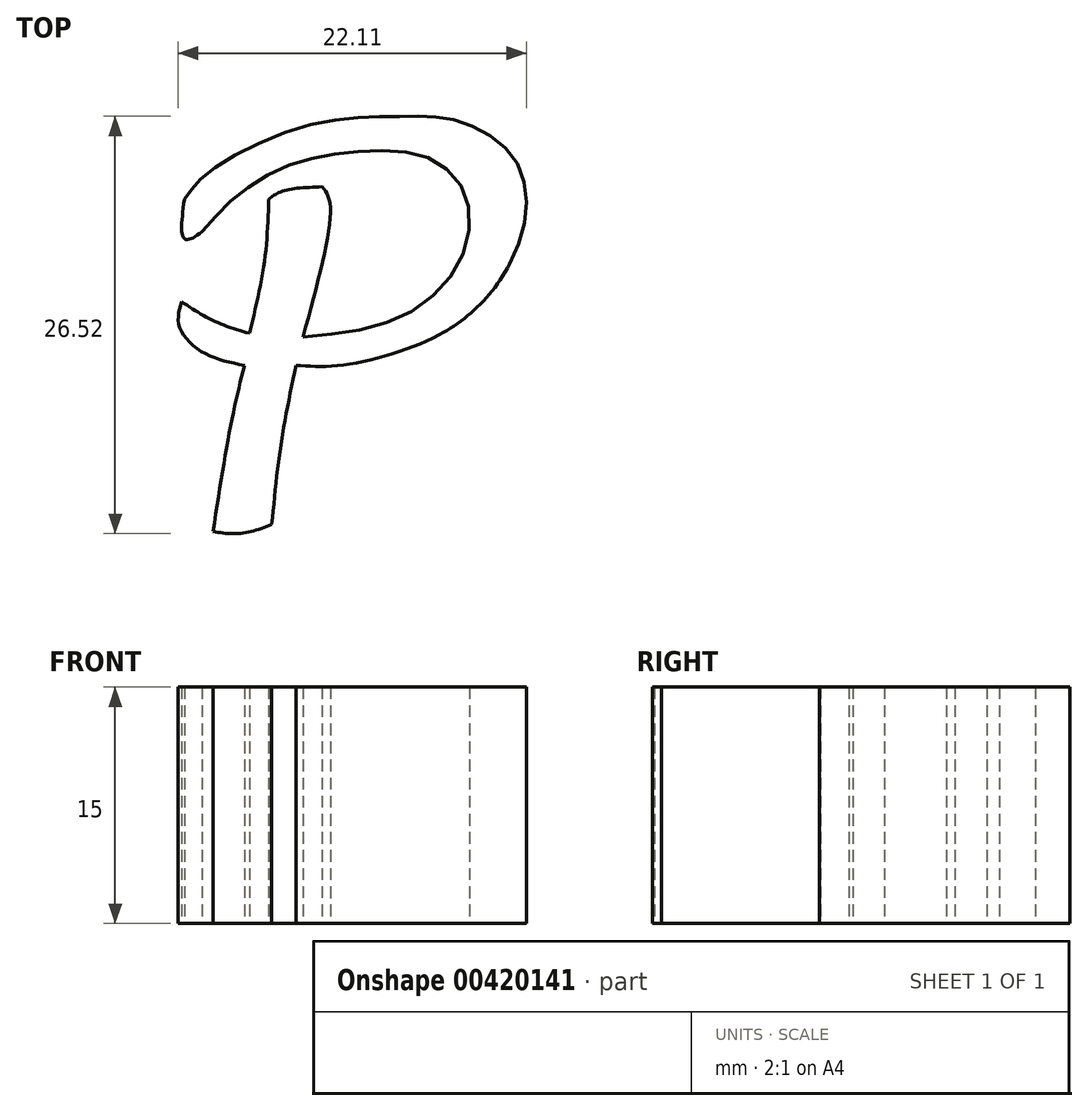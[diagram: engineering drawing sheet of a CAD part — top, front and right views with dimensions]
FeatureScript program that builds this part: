
annotation { "Feature Type Name" : "Feature", "Feature Type Description" : "" }
export const myFeature = defineFeature(function(context is Context, id is Id, definition is map)
    precondition{}
    {
        {
            var Q0;
            Q0=qCreatedBy(makeId("Top.planeOp"),FACE);
            var sketch = newSketch(context, id + "F0", { "sketchPlane" : qUnion([Q0])});
            skFitSpline(sketch, "E0", {"points": [v(-29.52, 16.09) * mm, v(-21.73, 24.17) * mm, v(-15.95, 22) * mm], "startDerivative": vector(5.63, 25.07) * mm, "endDerivative": vector(12.64, -16.05) * mm});
            skFitSpline(sketch, "E1", {"points": [v(-29.52, 16.09) * mm, v(-29.52, 11.79) * mm, v(-26.49, 8.08) * mm, v(-18.6, 8.9) * mm, v(-11.86, 14.14) * mm], "startDerivative": vector(-2.65, -20.74) * mm, "endDerivative": vector(20.85, 20.56) * mm});
            skFitSpline(sketch, "E2", {"points": [v(-15.95, 22) * mm, v(-15.95, 19.53) * mm, v(-19.6, 15.68) * mm, v(-26.31, 14.5) * mm], "startDerivative": vector(1.91, -9.63) * mm, "endDerivative": vector(-17.6, -0.63) * mm});
            skFitSpline(sketch, "E3", {"points": [v(-26.31, 14.5) * mm, v(-26.31, 12.31) * mm, v(-24.25, 10.14) * mm, v(-18.22, 11.13) * mm, v(-11.16, 17.2) * mm], "startDerivative": vector(-1.95, -12.78) * mm, "endDerivative": vector(19.15, 20.18) * mm});
            skFitSpline(sketch, "E4", {"points": [v(-11.16, 17.2) * mm, v(-8.94, 21.18) * mm, v(-5, 24.17) * mm, v(-0.8, 24.22) * mm, v(2.15, 22.9) * mm], "startDerivative": vector(7.17, 15.76) * mm, "endDerivative": vector(12.55, -6.92) * mm});
            skFitSpline(sketch, "E5", {"points": [v(2.15, 22.9) * mm, v(2.96, 23.95) * mm, v(5.9, 24.4) * mm], "startDerivative": vector(1.46, 2.97) * mm, "endDerivative": vector(5.76, 0.2) * mm});
            skFitSpline(sketch, "E6", {"points": [v(-11.86, 14.14) * mm, v(-11.86, 10.9) * mm, v(-9.94, 8.05) * mm, v(-6.14, 8.37) * mm], "startDerivative": vector(-1.2, -9.86) * mm, "endDerivative": vector(11.9, 3.41) * mm});
            skFitSpline(sketch, "E7", {"points": [v(-6.14, 8.37) * mm, v(-2.1, 12.17) * mm, v(0.93, 17.2) * mm], "startDerivative": vector(8.72, 7.18) * mm, "endDerivative": vector(5.42, 10.46) * mm});
            skFitSpline(sketch, "E8", {"points": [v(0.93, 17.2) * mm, v(0.93, 11.63) * mm, v(3.05, 8.96) * mm, v(6.72, 9.41) * mm, v(12.48, 14.14) * mm], "startDerivative": vector(-2.53, -22.33) * mm, "endDerivative": vector(18.4, 18.48) * mm});
            skFitSpline(sketch, "E9", {"points": [v(5.9, 24.4) * mm, v(4.28, 19.57) * mm, v(4.12, 12.84) * mm, v(5.03, 11.7) * mm, v(7.94, 12.57) * mm, v(12.9, 17.2) * mm], "startDerivative": vector(-8.65, -19.72) * mm, "endDerivative": vector(19.75, 21.62) * mm});
            skFitSpline(sketch, "E10", {"points": [v(12.9, 17.2) * mm, v(14.78, 20.91) * mm, v(18.92, 23.71) * mm, v(21.5, 24.4) * mm, v(24.04, 24.4) * mm, v(25.8, 23.42) * mm, v(26.53, 22.62) * mm, v(26.53, 21.34) * mm], "startDerivative": vector(7.3, 21.14) * mm, "endDerivative": vector(-1.85, -13.72) * mm});
            skFitSpline(sketch, "E11", {"points": [v(26.53, 21.34) * mm, v(25.28, 20.25) * mm, v(23.65, 19.61) * mm], "startDerivative": vector(-2.36, -2.44) * mm, "endDerivative": vector(-3.4, -1.02) * mm});
            skFitSpline(sketch, "E12", {"points": [v(23.65, 19.61) * mm, v(23.65, 21.34) * mm, v(22.59, 22.59) * mm, v(19.84, 22.59) * mm, v(16.5, 19.47) * mm, v(15.44, 17.2) * mm, v(15.32, 13.21) * mm, v(17.37, 9.82) * mm, v(20.92, 9.28) * mm, v(26.53, 12.94) * mm, v(29.59, 16.3) * mm], "startDerivative": vector(3.16, 25.43) * mm, "endDerivative": vector(23.14, 28.11) * mm});
            skFitSpline(sketch, "E13", {"points": [v(12.48, 14.14) * mm, v(12.48, 11.74) * mm, v(14.3, 8.6) * mm, v(16.78, 7.12) * mm, v(20.7, 7.08) * mm, v(24.82, 9.2) * mm, v(29.53, 13.7) * mm], "startDerivative": vector(-2.82, -18.44) * mm, "endDerivative": vector(21.23, 22.93) * mm});
            skFitSpline(sketch, "E14", {"points": [v(29.59, 16.3) * mm, v(30.44, 19.1) * mm, v(33.77, 22.87) * mm, v(38.3, 24.54) * mm, v(41.2, 24.05) * mm, v(42.85, 22.55) * mm, v(43.33, 20.19) * mm, v(41.47, 17.24) * mm, v(36.7, 14.68) * mm, v(32.8, 14.36) * mm], "startDerivative": vector(5.2, 27.04) * mm, "endDerivative": vector(-32.45, 0.66) * mm});
            skFitSpline(sketch, "E15", {"points": [v(32.8, 14.36) * mm, v(32.8, 12.43) * mm, v(34.32, 10.34) * mm, v(38.4, 10.26) * mm, v(45.36, 14.68) * mm, v(50.16, 20.77) * mm], "startDerivative": vector(-1.91, -14.46) * mm, "endDerivative": vector(16.23, 24.12) * mm});
            skFitSpline(sketch, "E16", {"points": [v(29.53, 13.7) * mm, v(29.53, 12.01) * mm, v(31.32, 8.9) * mm, v(35.92, 7.67) * mm, v(42.01, 9.84) * mm, v(46.54, 13.35) * mm, v(49.86, 17.2) * mm, v(51.72, 20.2) * mm], "startDerivative": vector(-2.56, -18.37) * mm, "endDerivative": vector(12.98, 22.51) * mm});
            skLineSegment(sketch, "E17", {"start": v(50.16, 20.77) * mm, "end": v(51.72, 20.2) * mm});
            skFitSpline(sketch, "E18", {"points": [v(-26.18, 16.08) * mm, v(-25.34, 19.37) * mm, v(-22.06, 22.5) * mm, v(-19.63, 22.7) * mm, v(-18.72, 21.74) * mm, v(-18.99, 19.53) * mm, v(-20.98, 17.43) * mm, v(-24.32, 16.09) * mm, v(-26.18, 16.08) * mm]});
            skFitSpline(sketch, "E19", {"points": [v(-8.92, 15.05) * mm, v(-8.16, 18.38) * mm, v(-5.66, 21.9) * mm, v(-2.78, 22.4) * mm, v(1.45, 20.49) * mm], "startDerivative": vector(1.92, 13.6) * mm, "endDerivative": vector(15.76, -8.92) * mm});
            skFitSpline(sketch, "E20", {"points": [v(-8.92, 15.05) * mm, v(-8.92, 12.3) * mm, v(-7.52, 10.82) * mm, v(-5.4, 11.59) * mm, v(-1.43, 16.26) * mm, v(1.45, 20.49) * mm], "startDerivative": vector(-2.38, -16.28) * mm, "endDerivative": vector(10.96, 16.58) * mm});
            skFitSpline(sketch, "E21", {"points": [v(32.96, 15.95) * mm, v(33.77, 19.4) * mm, v(37.64, 22.68) * mm, v(40.06, 22.25) * mm, v(40.28, 19.67) * mm, v(36.73, 16.81) * mm, v(32.96, 15.95) * mm]});
            skLineSegment(sketch, "E22", {"start": v(-26.49, 8.08) * mm, "end": v(-26.49, 0) * mm});
            skFitSpline(sketch, "E23", {"points": [v(-39.17, 6.72) * mm, v(-38.6, 11.78) * mm, v(-37.63, 16.84) * mm], "startDerivative": vector(0.97, 10.16) * mm, "endDerivative": vector(2.1, 10.07) * mm});
            skFitSpline(sketch, "E24", {"points": [v(-37.63, 16.84) * mm, v(-34.88, 16.84) * mm, v(-29.82, 18.18) * mm, v(-25.73, 20.94) * mm, v(-23.16, 25.68) * mm, v(-23.8, 30.03) * mm, v(-27.45, 32.4) * mm, v(-31.17, 32.65) * mm, v(-36.87, 32.08) * mm, v(-43.4, 28.94) * mm, v(-44.72, 27.4) * mm], "startDerivative": vector(32.12, -2.24) * mm, "endDerivative": vector(-16.47, -20.53) * mm});
            skFitSpline(sketch, "E25", {"points": [v(-44.72, 27.4) * mm, v(-44.72, 24.9) * mm, v(-43.59, 25.35) * mm], "startDerivative": vector(-0.9, -6.83) * mm, "endDerivative": vector(3.83, 3.23) * mm});
            skFitSpline(sketch, "E26", {"points": [v(-43.59, 25.35) * mm, v(-41.22, 27.74) * mm, v(-37.57, 29.72) * mm, v(-33.41, 30.43) * mm, v(-29.25, 30.04) * mm, v(-26.82, 27.48) * mm, v(-27.33, 23.26) * mm, v(-31.24, 19.8) * mm, v(-37.2, 18.65) * mm], "startDerivative": vector(19.6, 22.42) * mm, "endDerivative": vector(-42.14, -3.8) * mm});
            skFitSpline(sketch, "E27", {"points": [v(-37.2, 18.65) * mm, v(-35.46, 27.03) * mm, v(-35.97, 28.19) * mm], "startDerivative": vector(3.92, 14.3) * mm, "endDerivative": vector(-2.43, 3.12) * mm});
            skFitSpline(sketch, "E28", {"points": [v(-35.97, 28.19) * mm, v(-38.52, 27.9) * mm, v(-39.36, 27.39) * mm], "startDerivative": vector(-4.73, -0.2) * mm, "endDerivative": vector(-1.82, -1.5) * mm});
            skFitSpline(sketch, "E29", {"points": [v(-39.17, 6.72) * mm, v(-41.13, 6.17) * mm, v(-42.9, 6.28) * mm], "startDerivative": vector(-3.82, -1.4) * mm, "endDerivative": vector(-3.65, 0.53) * mm});
            skFitSpline(sketch, "E30", {"points": [v(-42.9, 6.28) * mm, v(-41.77, 13.06) * mm, v(-40.91, 16.84) * mm], "startDerivative": vector(1.97, 12.75) * mm, "endDerivative": vector(2.02, 8.15) * mm});
            skFitSpline(sketch, "E31", {"points": [v(-40.91, 16.84) * mm, v(-43.59, 17.7) * mm, v(-45.06, 19.36) * mm, v(-44.9, 20.89) * mm], "startDerivative": vector(-7.42, 1.53) * mm, "endDerivative": vector(1.61, 5.39) * mm});
            skFitSpline(sketch, "E32", {"points": [v(-44.9, 20.89) * mm, v(-42.9, 19.69) * mm, v(-40.59, 18.88) * mm], "startDerivative": vector(3.9, -2.64) * mm, "endDerivative": vector(4.7, -1.38) * mm});
            skFitSpline(sketch, "E33", {"points": [v(-40.59, 18.88) * mm, v(-39.64, 23.42) * mm, v(-39.36, 27.39) * mm], "startDerivative": vector(2.16, 8.87) * mm, "endDerivative": vector(0.27, 8.13) * mm});
            skSolve(sketch);
        }
        {
            var Q0;
            {var subQ1=sQuery(id+"F0.wireOp",EDGE,"E23");Q0=makeQuery(id+"F0.imprint","IMPRINT",FACE,{"disambiguationData":[TD([[makeQuery(id+"F0.imprint","IMPRINT",EDGE,{"derivedFrom":subQ1}),1.0]])]});}
            var Q1;
            {var subQ3=sQuery(id+"F0.wireOp",EDGE,"E0");Q1=makeQuery(id+"F0.imprint","IMPRINT",FACE,{"disambiguationData":[TD([[makeQuery(id+"F0.imprint","IMPRINT",EDGE,{"derivedFrom":subQ3}),-1.0]])]});}
            extrude(context, id + "F1", {"entities" : qUnion([Q0, Q1]), "depth" : 15 * mm});
        }
    });
